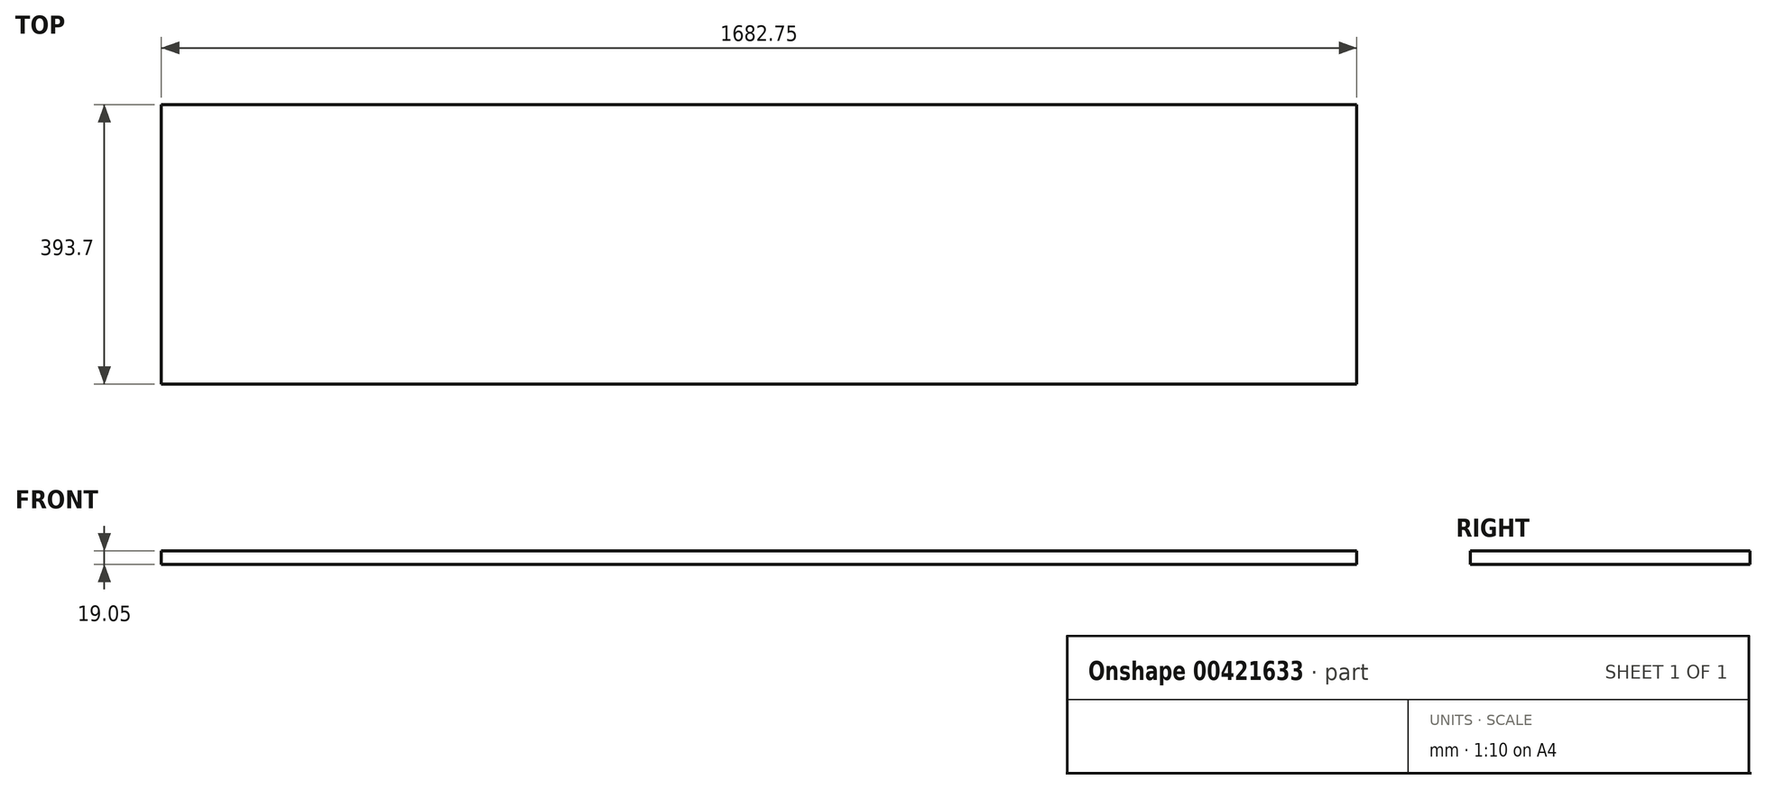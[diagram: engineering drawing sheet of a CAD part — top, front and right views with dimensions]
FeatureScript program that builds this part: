
annotation { "Feature Type Name" : "Feature", "Feature Type Description" : "" }
export const myFeature = defineFeature(function(context is Context, id is Id, definition is map)
    precondition{}
    {
        {
            var Q0;
            Q0=qCreatedBy(makeId("Front.planeOp"),FACE);
            var sketch = newSketch(context, id + "F0", { "sketchPlane" : qUnion([Q0])});
            skLineSegment(sketch, "E0.bottom", {"start": v(0, 0) * mm, "end": v(1682.75, 0) * mm});
            skLineSegment(sketch, "E0.top", {"start": v(0, 19.05) * mm, "end": v(1682.75, 19.05) * mm});
            skLineSegment(sketch, "E0.left", {"start": v(0, 0) * mm, "end": v(0, 19.05) * mm});
            skLineSegment(sketch, "E0.right", {"start": v(1682.75, 0) * mm, "end": v(1682.75, 19.05) * mm});
            skSolve(sketch);
        }
        {
            var Q0;
            Q0 = qSketchRegion(id + "F0", true);
            extrude(context, id + "F1", {"entities" : qUnion([Q0]), "depth" : 393.7 * mm});
        }
    });
